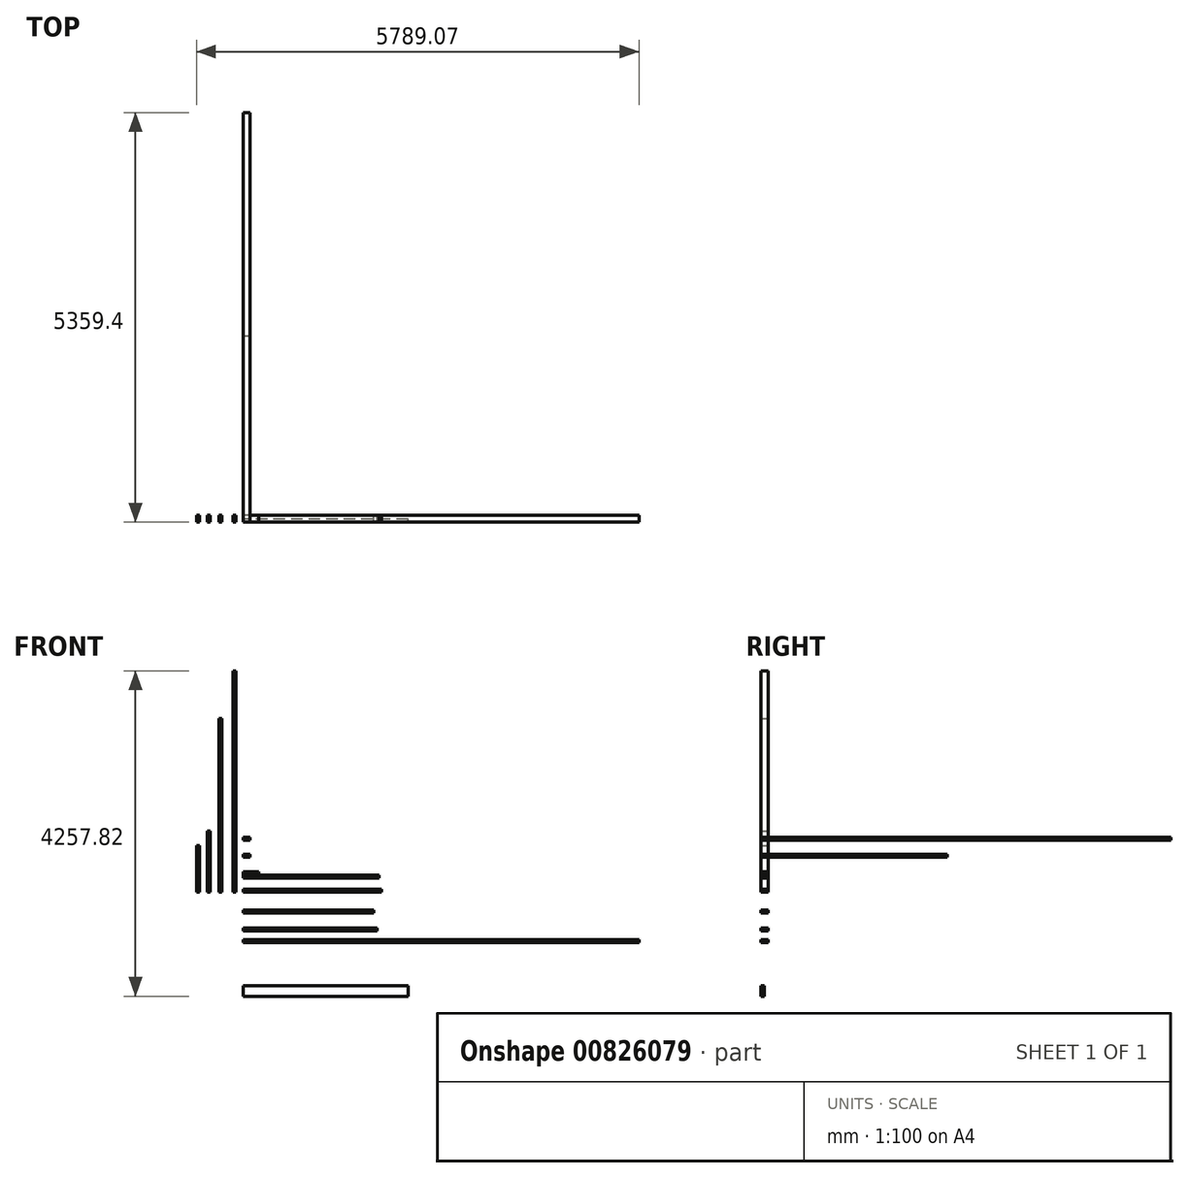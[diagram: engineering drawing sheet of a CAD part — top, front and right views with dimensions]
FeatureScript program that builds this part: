
annotation { "Feature Type Name" : "Feature", "Feature Type Description" : "" }
export const myFeature = defineFeature(function(context is Context, id is Id, definition is map)
    precondition{}
    {
        {
            var Q0;
            Q0=qCreatedBy(makeId("Right.planeOp"),FACE);
            var sketch = newSketch(context, id + "F0", { "sketchPlane" : qUnion([Q0])});
            skLineSegment(sketch, "E0.bottom", {"start": v(0, 0) * mm, "end": v(88.9, 0) * mm});
            skLineSegment(sketch, "E0.top", {"start": v(0, 38.1) * mm, "end": v(88.9, 38.1) * mm});
            skLineSegment(sketch, "E0.left", {"start": v(0, 0) * mm, "end": v(0, 38.1) * mm});
            skLineSegment(sketch, "E0.right", {"start": v(88.9, 0) * mm, "end": v(88.9, 38.1) * mm});
            skSolve(sketch);
        }
        {
            var Q0;
            Q0=qSketchRegion(id+"F0",true);
            extrude(context, id + "F1", {"entities" : qUnion([Q0]), "depth" : 1816.1 * mm, "offsetDistance" : 25.4 * mm});
        }
        {
            var Q0;
            Q0=qCreatedBy(makeId("Right.planeOp"),FACE);
            var sketch = newSketch(context, id + "F2", { "sketchPlane" : qUnion([Q0])});
            skLineSegment(sketch, "E1.bottom", {"start": v(0, 229.22) * mm, "end": v(88.9, 229.22) * mm});
            skLineSegment(sketch, "E1.top", {"start": v(0, 267.32) * mm, "end": v(88.9, 267.32) * mm});
            skLineSegment(sketch, "E1.left", {"start": v(0, 229.22) * mm, "end": v(0, 267.32) * mm});
            skLineSegment(sketch, "E1.right", {"start": v(88.9, 229.22) * mm, "end": v(88.9, 267.32) * mm});
            skSolve(sketch);
        }
        {
            var Q0;
            Q0=qSketchRegion(id+"F2",true);
            extrude(context, id + "F3", {"entities" : qUnion([Q0]), "depth" : ((18 * 12) - 7) * mm, "offsetDistance" : 25.4 * mm});
        }
        {
            var Q0;
            Q0=qCreatedBy(makeId("Top.planeOp"),FACE);
            var sketch = newSketch(context, id + "F4", { "sketchPlane" : qUnion([Q0])});
            skLineSegment(sketch, "E2.bottom", {"start": v(-93.15, 0) * mm, "end": v(-131.25, 0) * mm});
            skLineSegment(sketch, "E2.top", {"start": v(-93.15, 88.9) * mm, "end": v(-131.25, 88.9) * mm});
            skLineSegment(sketch, "E2.left", {"start": v(-93.15, 0) * mm, "end": v(-93.15, 88.9) * mm});
            skLineSegment(sketch, "E2.right", {"start": v(-131.25, 0) * mm, "end": v(-131.25, 88.9) * mm});
            skSolve(sketch);
        }
        {
            var Q0;
            Q0=qSketchRegion(id+"F4",true);
            extrude(context, id + "F5", {"entities" : qUnion([Q0]), "depth" : 2895.6 * mm, "offsetDistance" : 25.4 * mm});
        }
        {
            var Q0;
            Q0=qCreatedBy(makeId("Right.planeOp"),FACE);
            var sketch = newSketch(context, id + "F6", { "sketchPlane" : qUnion([Q0])});
            skLineSegment(sketch, "E3.bottom", {"start": v(0, 184.85) * mm, "end": v(88.9, 184.85) * mm});
            skLineSegment(sketch, "E3.top", {"start": v(0, 222.95) * mm, "end": v(88.9, 222.95) * mm});
            skLineSegment(sketch, "E3.left", {"start": v(0, 184.85) * mm, "end": v(0, 222.95) * mm});
            skLineSegment(sketch, "E3.right", {"start": v(88.9, 184.85) * mm, "end": v(88.9, 222.95) * mm});
            skSolve(sketch);
        }
        {
            var Q0;
            Q0=qSketchRegion(id+"F6",true);
            extrude(context, id + "F7", {"entities" : qUnion([Q0]), "depth" : 1778 * mm, "offsetDistance" : 25.4 * mm});
        }
        {
            var Q0;
            Q0=qCreatedBy(makeId("Top.planeOp"),FACE);
            var sketch = newSketch(context, id + "F8", { "sketchPlane" : qUnion([Q0])});
            skLineSegment(sketch, "E4.bottom", {"start": v(-276.06, 0) * mm, "end": v(-314.16, 0) * mm});
            skLineSegment(sketch, "E4.top", {"start": v(-276.06, 88.9) * mm, "end": v(-314.16, 88.9) * mm});
            skLineSegment(sketch, "E4.left", {"start": v(-276.06, 0) * mm, "end": v(-276.06, 88.9) * mm});
            skLineSegment(sketch, "E4.right", {"start": v(-314.16, 0) * mm, "end": v(-314.16, 88.9) * mm});
            skSolve(sketch);
        }
        {
            var Q0;
            Q0=qSketchRegion(id+"F8",true);
            extrude(context, id + "F9", {"entities" : qUnion([Q0]), "depth" : 2273.3 * mm, "offsetDistance" : 25.4 * mm});
        }
        {
            var Q0;
            Q0=qCreatedBy(makeId("Front.planeOp"),FACE);
            var sketch = newSketch(context, id + "F10", { "sketchPlane" : qUnion([Q0])});
            skLineSegment(sketch, "E5.bottom", {"start": v(0, 460.34) * mm, "end": v(88.9, 460.34) * mm});
            skLineSegment(sketch, "E5.top", {"start": v(0, 498.44) * mm, "end": v(88.9, 498.44) * mm});
            skLineSegment(sketch, "E5.left", {"start": v(0, 460.34) * mm, "end": v(0, 498.44) * mm});
            skLineSegment(sketch, "E5.right", {"start": v(88.9, 460.34) * mm, "end": v(88.9, 498.44) * mm});
            skSolve(sketch);
        }
        {
            var Q0;
            Q0=qSketchRegion(id+"F10",true);
            extrude(context, id + "F11", {"entities" : qUnion([Q0]), "oppositeDirection" : true, "depth" : 2438.4 * mm, "offsetDistance" : 25.4 * mm});
        }
        {
            var Q0;
            Q0=qCreatedBy(makeId("Top.planeOp"),FACE);
            var sketch = newSketch(context, id + "F12", { "sketchPlane" : qUnion([Q0])});
            skLineSegment(sketch, "E6.bottom", {"start": v(-569.37, 0) * mm, "end": v(-607.47, 0) * mm});
            skLineSegment(sketch, "E6.top", {"start": v(-569.37, 88.9) * mm, "end": v(-607.47, 88.9) * mm});
            skLineSegment(sketch, "E6.left", {"start": v(-569.37, 0) * mm, "end": v(-569.37, 88.9) * mm});
            skLineSegment(sketch, "E6.right", {"start": v(-607.47, 0) * mm, "end": v(-607.47, 88.9) * mm});
            skSolve(sketch);
        }
        {
            var Q0;
            Q0=qSketchRegion(id+"F12",true);
            extrude(context, id + "F13", {"entities" : qUnion([Q0]), "depth" : 609.6 * mm, "offsetDistance" : 25.4 * mm});
        }
        {
            var Q0;
            Q0=qCreatedBy(makeId("Top.planeOp"),FACE);
            var sketch = newSketch(context, id + "F14", { "sketchPlane" : qUnion([Q0])});
            skLineSegment(sketch, "E7.bottom", {"start": v(-430.54, 0) * mm, "end": v(-468.64, 0) * mm});
            skLineSegment(sketch, "E7.top", {"start": v(-430.54, 88.9) * mm, "end": v(-468.64, 88.9) * mm});
            skLineSegment(sketch, "E7.left", {"start": v(-430.54, 0) * mm, "end": v(-430.54, 88.9) * mm});
            skLineSegment(sketch, "E7.right", {"start": v(-468.64, 0) * mm, "end": v(-468.64, 88.9) * mm});
            skSolve(sketch);
        }
        {
            var Q0;
            Q0=qSketchRegion(id+"F14",true);
            extrude(context, id + "F15", {"entities" : qUnion([Q0]), "depth" : 800.1 * mm, "offsetDistance" : 25.4 * mm});
        }
        {
            var Q0;
            Q0=qCreatedBy(makeId("Front.planeOp"),FACE);
            var sketch = newSketch(context, id + "F16", { "sketchPlane" : qUnion([Q0])});
            skLineSegment(sketch, "E8.bottom", {"start": v(0, 678.63) * mm, "end": v(88.9, 678.63) * mm});
            skLineSegment(sketch, "E8.top", {"start": v(0, 716.73) * mm, "end": v(88.9, 716.73) * mm});
            skLineSegment(sketch, "E8.left", {"start": v(0, 678.63) * mm, "end": v(0, 716.73) * mm});
            skLineSegment(sketch, "E8.right", {"start": v(88.9, 678.63) * mm, "end": v(88.9, 716.73) * mm});
            skSolve(sketch);
        }
        {
            var Q0;
            Q0=qSketchRegion(id+"F16",true);
            extrude(context, id + "F17", {"entities" : qUnion([Q0]), "oppositeDirection" : true, "depth" : 5359.4 * mm, "offsetDistance" : 25.4 * mm});
        }
        {
            var Q0;
            Q0=qCreatedBy(makeId("Right.planeOp"),FACE);
            var sketch = newSketch(context, id + "F18", { "sketchPlane" : qUnion([Q0])});
            skLineSegment(sketch, "E9.bottom", {"start": v(0, -237.44) * mm, "end": v(88.9, -237.44) * mm});
            skLineSegment(sketch, "E9.top", {"start": v(0, -275.54) * mm, "end": v(88.9, -275.54) * mm});
            skLineSegment(sketch, "E9.left", {"start": v(0, -237.44) * mm, "end": v(0, -275.54) * mm});
            skLineSegment(sketch, "E9.right", {"start": v(88.9, -237.44) * mm, "end": v(88.9, -275.54) * mm});
            skSolve(sketch);
        }
        {
            var Q0;
            Q0=qSketchRegion(id+"F18",true);
            extrude(context, id + "F19", {"entities" : qUnion([Q0]), "depth" : 1714.5 * mm, "offsetDistance" : 25.4 * mm});
        }
        {
            var Q0;
            Q0=qCreatedBy(makeId("Right.planeOp"),FACE);
            var sketch = newSketch(context, id + "F20", { "sketchPlane" : qUnion([Q0])});
            skLineSegment(sketch, "E10.bottom", {"start": v(0, -623.77) * mm, "end": v(88.9, -623.77) * mm});
            skLineSegment(sketch, "E10.top", {"start": v(0, -661.87) * mm, "end": v(88.9, -661.87) * mm});
            skLineSegment(sketch, "E10.left", {"start": v(0, -623.77) * mm, "end": v(0, -661.87) * mm});
            skLineSegment(sketch, "E10.right", {"start": v(88.9, -623.77) * mm, "end": v(88.9, -661.87) * mm});
            skSolve(sketch);
        }
        {
            var Q0;
            Q0=qSketchRegion(id+"F20",true);
            extrude(context, id + "F21", {"entities" : qUnion([Q0]), "depth" : 5181.6 * mm, "offsetDistance" : 25.4 * mm});
        }
        {
            var Q0;
            Q0=qCreatedBy(makeId("Right.planeOp"),FACE);
            var sketch = newSketch(context, id + "F22", { "sketchPlane" : qUnion([Q0])});
            skLineSegment(sketch, "E11.bottom", {"start": v(0, -504.94) * mm, "end": v(88.9, -504.94) * mm});
            skLineSegment(sketch, "E11.top", {"start": v(0, -466.84) * mm, "end": v(88.9, -466.84) * mm});
            skLineSegment(sketch, "E11.left", {"start": v(0, -504.94) * mm, "end": v(0, -466.84) * mm});
            skLineSegment(sketch, "E11.right", {"start": v(88.9, -504.94) * mm, "end": v(88.9, -466.84) * mm});
            skSolve(sketch);
        }
        {
            var Q0;
            Q0=qSketchRegion(id+"F22",true);
            extrude(context, id + "F23", {"entities" : qUnion([Q0]), "depth" : 1752.6 * mm, "offsetDistance" : 25.4 * mm});
        }
        {
            var Q0;
            Q0=qCreatedBy(makeId("Right.planeOp"),FACE);
            var sketch = newSketch(context, id + "F24", { "sketchPlane" : qUnion([Q0])});
            skLineSegment(sketch, "E12.bottom", {"start": v(0, -1222.52) * mm, "end": v(38.1, -1222.52) * mm});
            skLineSegment(sketch, "E12.top", {"start": v(0, -1362.22) * mm, "end": v(38.1, -1362.22) * mm});
            skLineSegment(sketch, "E12.left", {"start": v(0, -1222.52) * mm, "end": v(0, -1362.22) * mm});
            skLineSegment(sketch, "E12.right", {"start": v(38.1, -1222.52) * mm, "end": v(38.1, -1362.22) * mm});
            skSolve(sketch);
        }
        {
            var Q0;
            Q0 = qSketchRegion(id + "F24", true);
            extrude(context, id + "F25", {"entities" : qUnion([Q0]), "depth" : 2159 * mm, "offsetDistance" : 25.4 * mm});
        }
    });
